# Revit family: Drain_Floor_Deck_9_Inch_Round-Zurn-Z530-Wide-Flange-Medium-Duty
name_source: partatom
category: Plumbing Fixtures
units: mm (PartAtom-declared; Revit-internal decimal feet)

## family parameters
Always vertical = Yes
Cut with Voids When Loaded = No
Maintain Annotation Orientation = No
OmniClass Number = 23.70.50.21.24.14
OmniClass Title = Deck Waste Water Drains
Part Type = Normal
Room Calculation Point = No
Round Connector Dimension = Use Radius
Shared = No
Work Plane-Based = No

## types (9) — shared parameters
Approx. Wt. Lbs. = 49 "
Assembly Code = D2030300
CW Connection = No
Default Elevation = 20 "
Description = 9 [229] MEDIUM-DUTY WIDE FLANGE DECK DRAIN
Grate Open Area Sq.in = 18 "
HW Connection = No
HWFU = 1
Main Material = Iron - Zurn -Cast - Painted - Blue
Manufacturer = Zurn Water, LLC
Manufacturer Brand = Zurn
Model = Z530
Modified Date = 12/19/2025
Product Documentation Link = https://files.zurn.com
Product Page URL = https://www.zurn.com
Product data URL = https://www.bimobject.com
Top Diameter = 17 "
URL = www.zurn.com
Vent Connection = No
Waste Connection = Yes
Wide flange Deck Diameter = 9 "
zero-valued in all types: CWFU, WFU

## per-type parameters (varying)
| type | Body Height_E | Connector Radius | Pipe Size_A Inside Diameter | Pipe Size_A Nominal Diameter | Pipe Size_A Outer Diameter | Type Comments |
| Z530-2IC | 5.5 " | 1 " | 2.067 " | 2 " | 2.375 " | Z530-2 Inch Inside Caulk Outlet |
| Z530-3IC | 5.5 " | 1.5 " | 3.068 " | 3 " | 3.5 " | Z530-3 Inch Inside Caulk Outlet |
| Z530-4IC | 5.5 " | 2 " | 4.026 " | 4 " | 4.5 " | Z530-4 Inch Inside Caulk Outlet |
| Z530-2IP | 4 " | 1 " | 2.067 " | 2 " | 2.375 " | Z530-2 Inch Threaded Outlet |
| Z530-3IP | 4 " | 1.5 " | 3.068 " | 3 " | 3.5 " | Z530-3 Inch Threaded Outlet |
| Z530-4IP | 4 " | 2 " | 4.026 " | 4 " | 4.5 " | Z530-4 Inch Threaded Outlet |
| Z530-2NL | 4.75 " | 1 " | 2.067 " | 2 " | 2.375 " | Z530-2 Inch Neo-Loc Outlet |
| Z530-3NL | 4.75 " | 1.5 " | 3.068 " | 3 " | 3.5 " | Z530-3 Inch Neo-Loc Outlet |
| Z530-4NL | 4.75 " | 2 " | 4.026 " | 4 " | 4.5 " | Z530-4 Inch Neo-Loc Outlet |

## geometry (parser evidence)
native form markers: Sweep x3
no freeform markers — native parametric forms only
